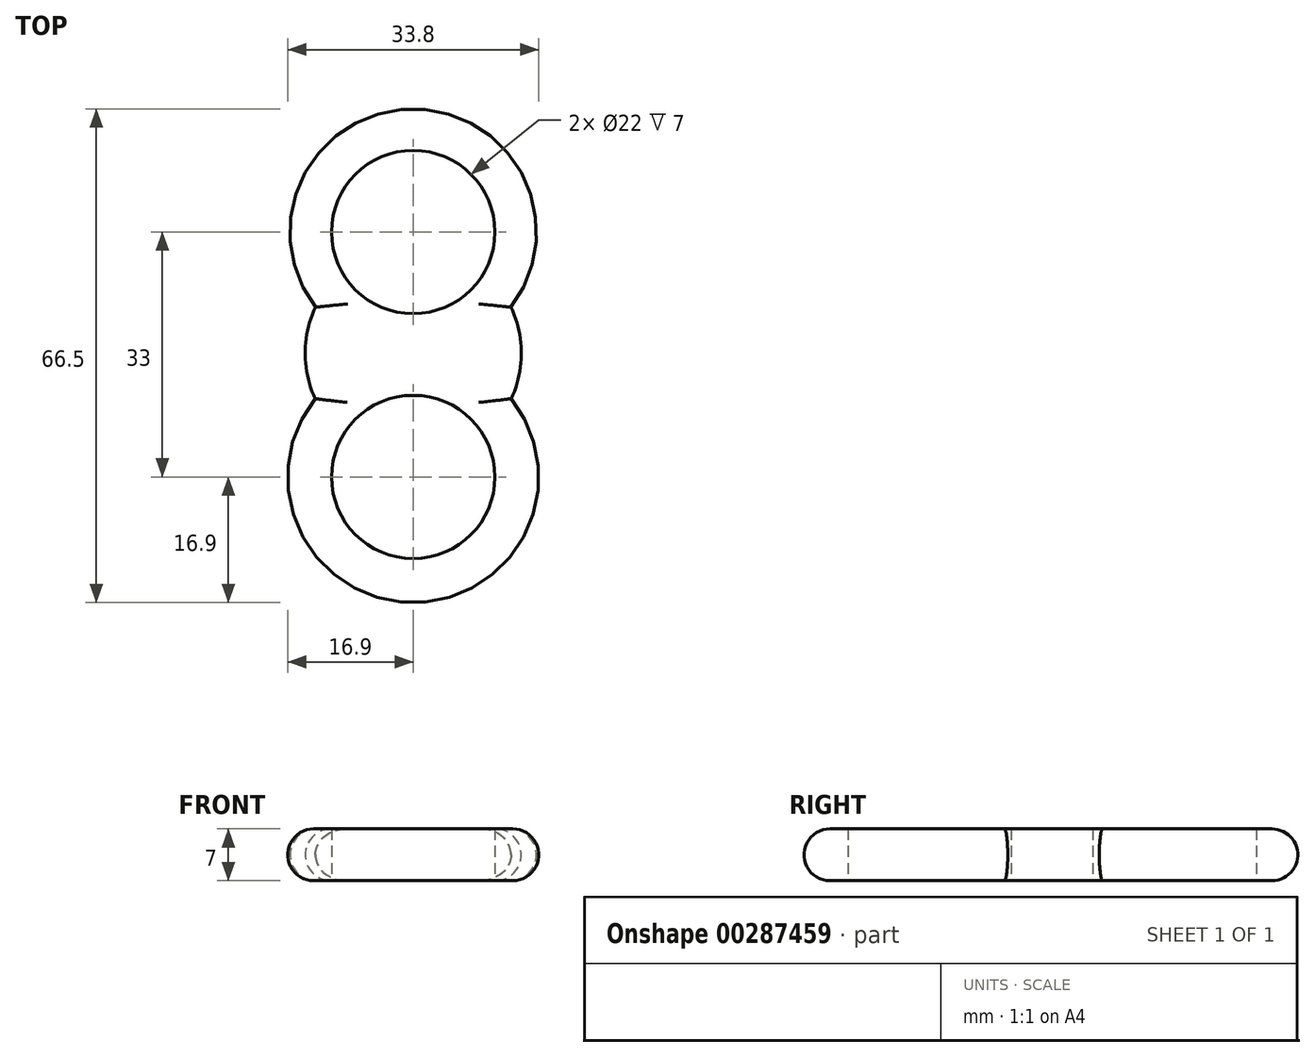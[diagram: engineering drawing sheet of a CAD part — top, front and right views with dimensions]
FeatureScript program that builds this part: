
annotation { "Feature Type Name" : "Feature", "Feature Type Description" : "" }
export const myFeature = defineFeature(function(context is Context, id is Id, definition is map)
    precondition{}
    {
        {
            var Q0;
            Q0=qCreatedBy(makeId("Top.planeOp"),FACE);
            var sketch = newSketch(context, id + "F0", { "sketchPlane" : qUnion([Q0])});
            skCircle(sketch, "E0", {"center": v(0, 0) * mm, "radius": 11 * mm});
            skCircle(sketch, "E1", {"center": v(0, 33) * mm, "radius": 11 * mm});
            skArc(sketch, "E2", {"start": v(13.15, 22.88) * mm, "mid": v(0, 49.6) * mm, "end": v(-13.15, 22.88) * mm});
            skLineSegment(sketch, "E3", {"start": v(0, 16.9) * mm, "end": v(0, 16.65) * mm});
            skArc(sketch, "E4", {"start": v(-13.15, 22.88) * mm, "mid": v(-14.55, 16.72) * mm, "end": v(-13.2, 10.55) * mm});
            skArc(sketch, "E5.trimOffspring", {"start": v(13.2, 10.55) * mm, "mid": v(14.55, 16.72) * mm, "end": v(13.15, 22.88) * mm});
            skArc(sketch, "E6.trimOffspring", {"start": v(-13.2, 10.55) * mm, "mid": v(0, -16.9) * mm, "end": v(13.2, 10.55) * mm});
            skPoint(sketch, "E7.orphan", {"position": v(0, 16.4) * mm});
            skSolve(sketch);
        }
        {
            var Q0;
            Q0 = qSketchRegion(id + "F0", true);
            extrude(context, id + "F1", {"entities" : qUnion([Q0]), "depth" : 7 * mm});
        }
        {
            var Q0;
            Q0=makeQuery(id+"F1.opExtrude","CAP_EDGE",EDGE,{"disambiguationData":[OSD([sQuery(id+"F0.wireOp",EDGE,"E2")])],"isStart":false});
            var Q1;
            Q1=makeQuery(id+"F1.opExtrude","CAP_EDGE",EDGE,{"disambiguationData":[OSD([sQuery(id+"F0.wireOp",EDGE,"E4")])],"isStart":false});
            var Q2;
            Q2=makeQuery(id+"F1.opExtrude","CAP_EDGE",EDGE,{"disambiguationData":[OSD([sQuery(id+"F0.wireOp",EDGE,"E6.trimOffspring")])],"isStart":false});
            var Q3;
            Q3=makeQuery(id+"F1.opExtrude","CAP_EDGE",EDGE,{"disambiguationData":[OSD([sQuery(id+"F0.wireOp",EDGE,"E5.trimOffspring")])],"isStart":false});
            var Q4;
            Q4=makeQuery(id+"F1.opExtrude","CAP_EDGE",EDGE,{"disambiguationData":[OSD([sQuery(id+"F0.wireOp",EDGE,"E5.trimOffspring")])],"isStart":true});
            var Q5;
            Q5=makeQuery(id+"F1.opExtrude","CAP_EDGE",EDGE,{"disambiguationData":[OSD([sQuery(id+"F0.wireOp",EDGE,"E2")])],"isStart":true});
            var Q6;
            Q6=makeQuery(id+"F1.opExtrude","CAP_EDGE",EDGE,{"disambiguationData":[OSD([sQuery(id+"F0.wireOp",EDGE,"E6.trimOffspring")])],"isStart":true});
            var Q7;
            Q7=makeQuery(id+"F1.opExtrude","CAP_EDGE",EDGE,{"disambiguationData":[OSD([sQuery(id+"F0.wireOp",EDGE,"E4")])],"isStart":true});
            fillet(context, id + "F2", {"entities" : qUnion([Q0, Q1, Q2, Q3, Q4, Q5, Q6, Q7]), "radius" : 3.5 * mm, "tangentPropagation" : true, "allowEdgeOverflow" : false});
        }
    });
